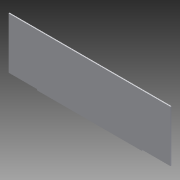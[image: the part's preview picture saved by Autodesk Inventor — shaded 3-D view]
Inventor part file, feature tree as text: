
AUTODESK INVENTOR PART (.ipt)
format: ipt  version: 2012 (Build 160160000, 160)  size: 74,240 bytes
history: native  units: in
note: dims shown in document units (in); Inventor stores cm internally (conversion verified against a paired STEP export)
features: extrude x1, sketch x1
ambient origin geometry x8: Origin, YZ Plane, XZ Plane, XY Plane, X Axis, Y Axis, Z Axis, Center Point
bodies: Solid1 (feature_tree)
feature tree (2):
  extrude  "Extrusion1"  Depth=37.0in
  sketch  "Sketch1"  dims[d0=12.0in d1=37.0in d2=6.5in d3=0.25in d4=0.25in d5=0.0in]
